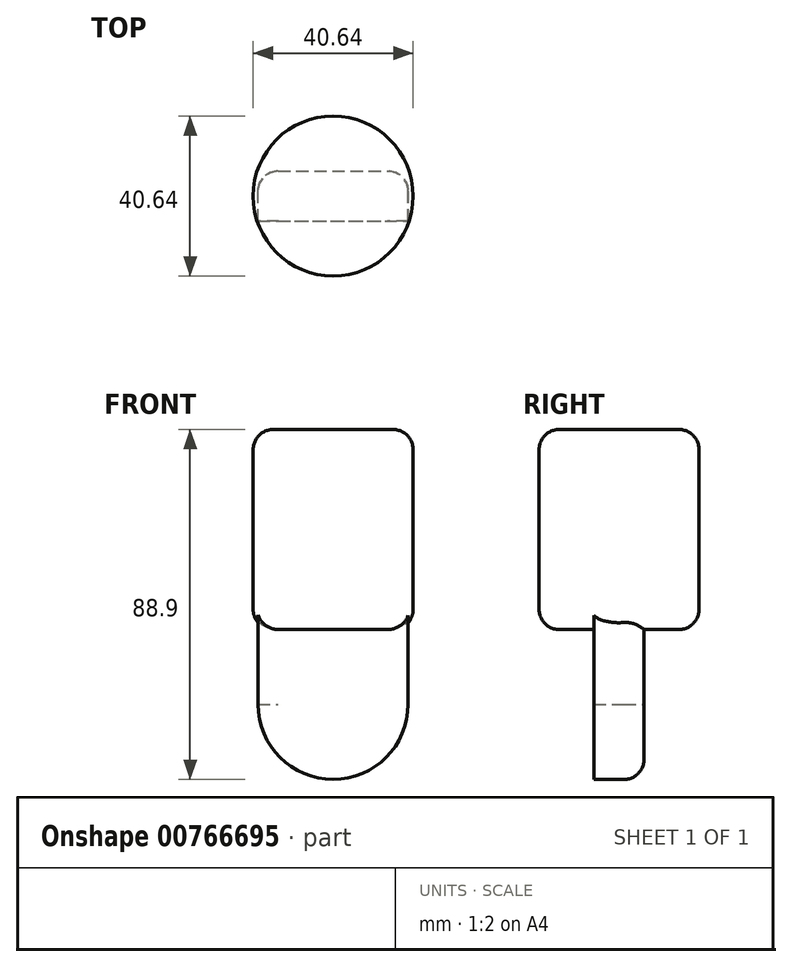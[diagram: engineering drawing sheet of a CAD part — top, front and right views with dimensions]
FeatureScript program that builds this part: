
annotation { "Feature Type Name" : "Feature", "Feature Type Description" : "" }
export const myFeature = defineFeature(function(context is Context, id is Id, definition is map)
    precondition{}
    {
        {
            var Q0;
            Q0=qCreatedBy(makeId("Front.planeOp"),FACE);
            var sketch = newSketch(context, id + "F0", { "sketchPlane" : qUnion([Q0])});
            skCircle(sketch, "E0", {"center": v(0, 0) * mm, "radius": 19.05 * mm});
            skLineSegment(sketch, "E1", {"start": v(0, 19.05) * mm, "end": v(0, 69.85) * mm});
            skLineSegment(sketch, "E2", {"start": v(0, 19.05) * mm, "end": v(20.32, 19.05) * mm});
            skLineSegment(sketch, "E3", {"start": v(20.32, 19.05) * mm, "end": v(20.32, 69.85) * mm});
            skLineSegment(sketch, "E4", {"start": v(20.32, 69.85) * mm, "end": v(0, 69.85) * mm});
            skLineSegment(sketch, "E5", {"start": v(0, 19.05) * mm, "end": v(-20.32, 19.05) * mm});
            skLineSegment(sketch, "E6", {"start": v(0, 0) * mm, "end": v(-19.09, 0) * mm});
            skLineSegment(sketch, "E7", {"start": v(0, 0) * mm, "end": v(19.05, 0) * mm});
            skLineSegment(sketch, "E8", {"start": v(19.05, 0) * mm, "end": v(19.05, 19.05) * mm});
            skLineSegment(sketch, "E9", {"start": v(-19.09, 0) * mm, "end": v(-19.09, 19.05) * mm});
            skSolve(sketch);
        }
        {
            var Q0;
            {var subQ3=sQuery(id+"F0.wireOp",EDGE,"E8");Q0=makeQuery(id+"F0.imprint","IMPRINT",FACE,{"disambiguationData":[TD([[makeQuery(id+"F0.imprint","IMPRINT",EDGE,{"derivedFrom":subQ3}),1.0]])]});}
            var Q1;
            {var subQ2=sQuery(id+"F0.wireOp",EDGE,"E7");Q1=makeQuery(id+"F0.imprint","IMPRINT",FACE,{"disambiguationData":[TD([[makeQuery(id+"F0.imprint","IMPRINT",EDGE,{"derivedFrom":subQ2}),1.0]])]});}
            var Q2;
            {var subQ5=sQuery(id+"F0.wireOp",EDGE,"E9");Q2=makeQuery(id+"F0.imprint","IMPRINT",FACE,{"disambiguationData":[TD([[makeQuery(id+"F0.imprint","IMPRINT",EDGE,{"derivedFrom":subQ5}),-1.0]])]});}
            var Q3;
            {var subQ0=sQuery(id+"F0.wireOp",EDGE,"E7");Q3=makeQuery(id+"F0.imprint","IMPRINT",FACE,{"disambiguationData":[TD([[makeQuery(id+"F0.imprint","IMPRINT",EDGE,{"derivedFrom":subQ0}),-1.0]])]});}
            extrude(context, id + "F1", {"entities" : qUnion([Q0, Q1, Q2, Q3]), "endBound" : BoundingType.SYMMETRIC, "depth" : 12.7 * mm, "offsetDistance" : 25.4 * mm});
        }
        {
            var Q0;
            {var subQ3=sQuery(id+"F0.wireOp",EDGE,"E1");Q0=makeQuery(id+"F0.imprint","IMPRINT",FACE,{"disambiguationData":[TD([[makeQuery(id+"F0.imprint","IMPRINT",EDGE,{"derivedFrom":subQ3}),-1.0]])]});}
            var Q1;
            Q1=sQuery(id+"F0.wireOp",EDGE,"E1");
            revolve(context, id + "F2", {"operationType" : NewBodyOperationType.ADD, "surfaceOperationType" : NewSurfaceOperationType.NEW, "entities" : qUnion([Q0]), "axis" : qUnion([Q1]), "revolveType" : RevolveType.FULL});
        }
        {
            var Q0;
            Q0=makeQuery(id+"F1.opExtrude","CAP_EDGE",EDGE,{"disambiguationData":[OSD([sQuery(id+"F0.wireOp",EDGE,"E0")])],"isStart":true});
            var Q1;
            Q1=makeQuery(id+"F1.opExtrude","CAP_EDGE",EDGE,{"disambiguationData":[OSD([sQuery(id+"F0.wireOp",EDGE,"E8")])],"isStart":true});
            fillet(context, id + "F3", {"entities" : qUnion([Q0, Q1]), "radius" : 5.08 * mm, "tangentPropagation" : true, "allowEdgeOverflow" : false});
        }
        {
            var Q0;
            Q0=makeQuery(id+"F1.opExtrude","CAP_EDGE",EDGE,{"disambiguationData":[OSD([sQuery(id+"F0.wireOp",EDGE,"E9")])],"isStart":true});
            fillet(context, id + "F4", {"entities" : qUnion([Q0]), "radius" : 5.08 * mm, "tangentPropagation" : true, "allowEdgeOverflow" : false});
        }
        {
            var Q0;
            Q0=makeQuery(id+"F2.opRevolve","SWEPT_EDGE",EDGE,{"disambiguationData":[OSD([sQuery(id+"F0.wireOp",EDGE,"E2"),sQuery(id+"F0.wireOp",EDGE,"E3")])]});
            fillet(context, id + "F5", {"entities" : qUnion([Q0]), "radius" : 5.08 * mm, "tangentPropagation" : true, "allowEdgeOverflow" : false});
        }
        {
            var Q0;
            Q0=makeQuery(id+"F2.opRevolve","SWEPT_EDGE",EDGE,{"disambiguationData":[OSD([sQuery(id+"F0.wireOp",EDGE,"E3"),sQuery(id+"F0.wireOp",EDGE,"E4")])]});
            fillet(context, id + "F6", {"entities" : qUnion([Q0]), "radius" : 5.08 * mm, "tangentPropagation" : true, "allowEdgeOverflow" : false});
        }
    });
